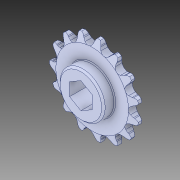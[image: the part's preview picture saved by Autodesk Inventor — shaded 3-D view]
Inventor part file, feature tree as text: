
AUTODESK INVENTOR PART (.ipt)
format: ipt  version: 2019 (Build 230136000, 136)  size: 466,432 bytes
history: native  units: in
note: dims shown in document units (in); Inventor stores cm internally (conversion verified against a paired STEP export)
features: chamfer x1
ambient origin geometry x8: Origin, YZ Plane, XZ Plane, XY Plane, X Axis, Y Axis, Z Axis, Center Point
bodies: Solid1 (feature_tree)
feature tree (1):
  chamfer  "Chamfer1"  [1 undecoded]
note: 1 required parameter value undecoded (feature->parameter linkage not recoverable at this tier; creation-order binding heuristic only, values carry confidence <= 0.55)
